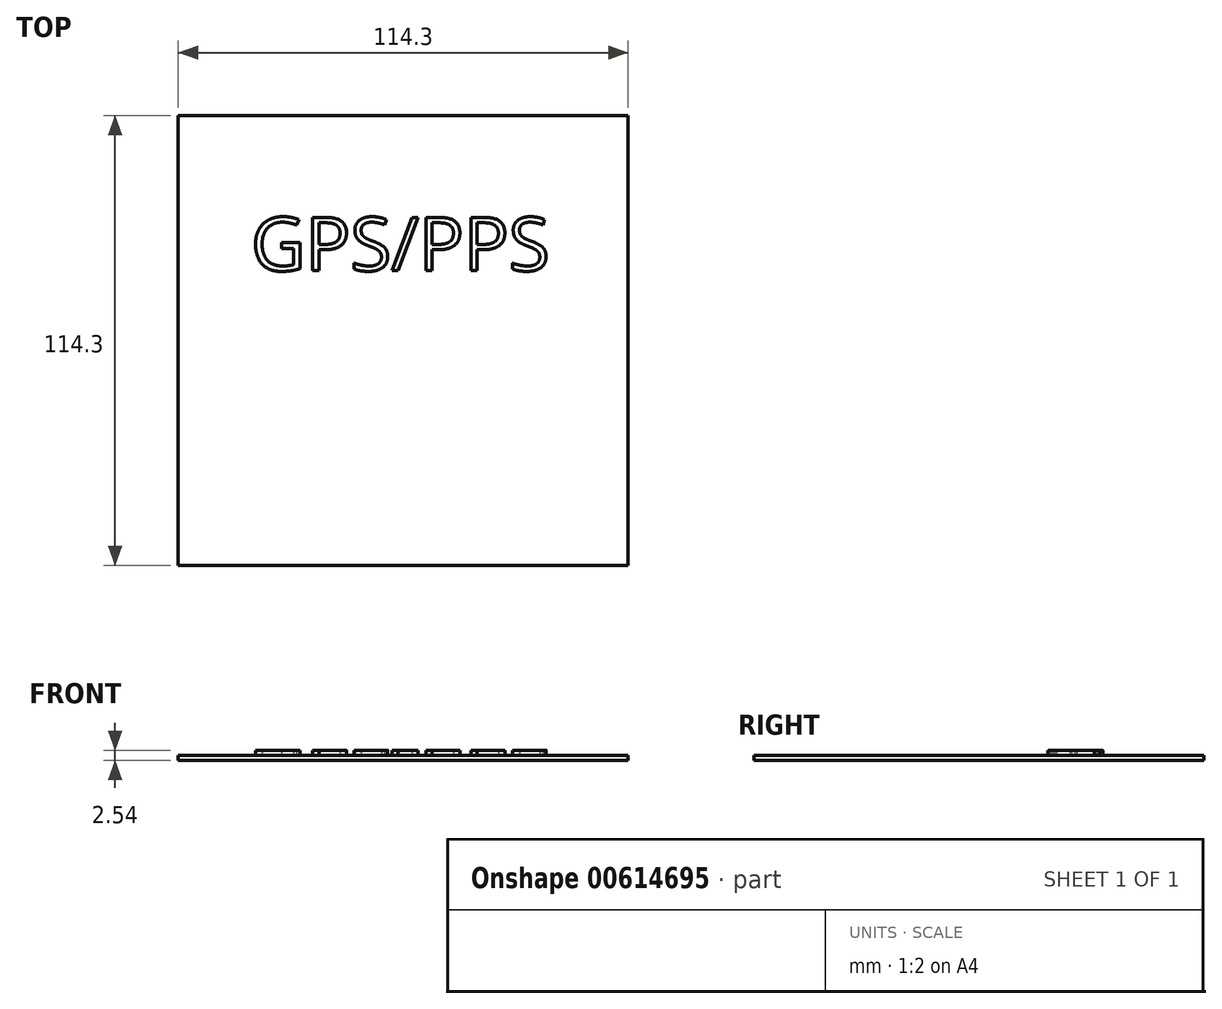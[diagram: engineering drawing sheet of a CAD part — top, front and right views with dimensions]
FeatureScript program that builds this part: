
annotation { "Feature Type Name" : "Feature", "Feature Type Description" : "" }
export const myFeature = defineFeature(function(context is Context, id is Id, definition is map)
    precondition{}
    {
        {
            var Q0;
            Q0=qCreatedBy(makeId("Top.planeOp"),FACE);
            var sketch = newSketch(context, id + "F0", { "sketchPlane" : qUnion([Q0])});
            skLineSegment(sketch, "E0.bottom", {"start": v(-54.69, 67.69) * mm, "end": v(59.61, 67.69) * mm});
            skLineSegment(sketch, "E0.top", {"start": v(-54.69, -46.61) * mm, "end": v(59.61, -46.61) * mm});
            skLineSegment(sketch, "E0.left", {"start": v(-54.69, 67.69) * mm, "end": v(-54.69, -46.61) * mm});
            skLineSegment(sketch, "E0.right", {"start": v(59.61, 67.69) * mm, "end": v(59.61, -46.61) * mm});
            skSolve(sketch);
        }
        {
            var Q0;
            Q0=makeQuery(id+"F0.imprint","IMPRINT",FACE,{"disambiguationData":[TD([[makeQuery(id+"F0.imprint","IMPRINT",EDGE,{"derivedFrom":sQuery(id+"F0.wireOp",EDGE,"E0.bottom")}),-1.0]])]});
            extrude(context, id + "F1", {"entities" : qUnion([Q0]), "depth" : 1.27 * mm, "offsetDistance" : 25.4 * mm});
        }
        {
            var Q0;
            Q0=makeQuery(id+"F1.opExtrude","CAP_FACE",FACE,{"disambiguationData":[OSD([sQuery(id+"F0.wireOp",EDGE,"E0.bottom"),sQuery(id+"F0.wireOp",EDGE,"E0.top"),sQuery(id+"F0.wireOp",EDGE,"E0.left"),sQuery(id+"F0.wireOp",EDGE,"E0.right")])],"isStart":false});
            var sketch = newSketch(context, id + "F2", { "sketchPlane" : qUnion([Q0])});
            skText(sketch, "E1", { "text": "GPS/PPS", "fontName": "OpenSans-Regular.ttf"});
            const initialGuessF2  = {"E1": [-0.0362, 0.02826, 1, 0, 0.01366]};
            skSetInitialGuess(sketch, initialGuessF2);
            skSolve(sketch);
        }
        {
            var Q0;
            Q0 = qSketchRegion(id + "F2", true);
            extrude(context, id + "F3", {"entities" : qUnion([Q0]), "operationType" : NewBodyOperationType.ADD, "depth" : 1.27 * mm, "offsetDistance" : 25.4 * mm});
        }
    });
